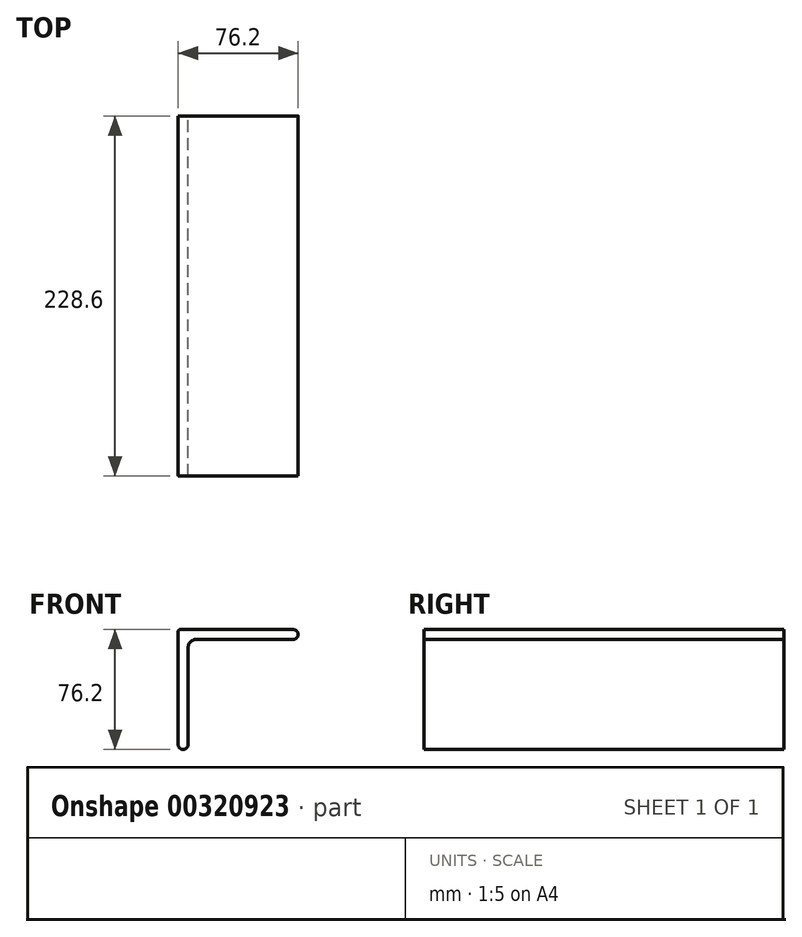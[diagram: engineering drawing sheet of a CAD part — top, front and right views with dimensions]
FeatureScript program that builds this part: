
annotation { "Feature Type Name" : "Feature", "Feature Type Description" : "" }
export const myFeature = defineFeature(function(context is Context, id is Id, definition is map)
    precondition{}
    {
        {
            var Q0;
            Q0=qCreatedBy(makeId("Front.planeOp"),FACE);
            var sketch = newSketch(context, id + "F0", { "sketchPlane" : qUnion([Q0])});
            skLineSegment(sketch, "E0", {"start": v(0, 0) * mm, "end": v(0, -76.2) * mm});
            skLineSegment(sketch, "E1", {"start": v(0, -76.2) * mm, "end": v(6.35, -76.2) * mm});
            skLineSegment(sketch, "E2", {"start": v(6.35, -76.2) * mm, "end": v(6.35, -6.35) * mm});
            skLineSegment(sketch, "E3", {"start": v(6.35, -6.35) * mm, "end": v(76.2, -6.35) * mm});
            skLineSegment(sketch, "E4", {"start": v(76.2, -6.35) * mm, "end": v(76.2, 0) * mm});
            skLineSegment(sketch, "E5", {"start": v(76.2, 0) * mm, "end": v(0, 0) * mm});
            skSolve(sketch);
        }
        {
            var Q0;
            Q0 = qSketchRegion(id + "F0", true);
            extrude(context, id + "F1", {"entities" : qUnion([Q0]), "endBound" : BoundingType.SYMMETRIC, "depth" : 228.6 * mm});
        }
        {
            var Q0;
            Q0=makeQuery(id+"F1.opExtrude","SWEPT_EDGE",EDGE,{"disambiguationData":[OSD([sQuery(id+"F0.wireOp",EDGE,"E2"),sQuery(id+"F0.wireOp",EDGE,"E3")])]});
            fillet(context, id + "F2", {"entities" : qUnion([Q0]), "radius" : 5.08 * mm, "tangentPropagation" : true, "allowEdgeOverflow" : false});
        }
        {
            var Q0;
            Q0=makeQuery(id+"F1.opExtrude","SWEPT_EDGE",EDGE,{"disambiguationData":[OSD([sQuery(id+"F0.wireOp",EDGE,"E3"),sQuery(id+"F0.wireOp",EDGE,"E4")])]});
            var Q1;
            Q1=makeQuery(id+"F1.opExtrude","SWEPT_EDGE",EDGE,{"disambiguationData":[OSD([sQuery(id+"F0.wireOp",EDGE,"E4"),sQuery(id+"F0.wireOp",EDGE,"E5")])]});
            var Q2;
            Q2=makeQuery(id+"F1.opExtrude","SWEPT_EDGE",EDGE,{"disambiguationData":[OSD([sQuery(id+"F0.wireOp",EDGE,"E0"),sQuery(id+"F0.wireOp",EDGE,"E1")])]});
            var Q3;
            Q3=makeQuery(id+"F1.opExtrude","SWEPT_EDGE",EDGE,{"disambiguationData":[OSD([sQuery(id+"F0.wireOp",EDGE,"E1"),sQuery(id+"F0.wireOp",EDGE,"E2")])]});
            fillet(context, id + "F3", {"entities" : qUnion([Q0, Q1, Q2, Q3]), "radius" : 3.17 * mm, "tangentPropagation" : true, "allowEdgeOverflow" : false});
        }
        {
            var Q0;
            Q0=makeQuery(id+"F1.opExtrude","SWEPT_EDGE",EDGE,{"disambiguationData":[OSD([sQuery(id+"F0.wireOp",EDGE,"E0"),sQuery(id+"F0.wireOp",EDGE,"E5")])]});
            fillet(context, id + "F4", {"entities" : qUnion([Q0]), "radius" : 1.4 * mm, "tangentPropagation" : true, "allowEdgeOverflow" : false});
        }
    });
